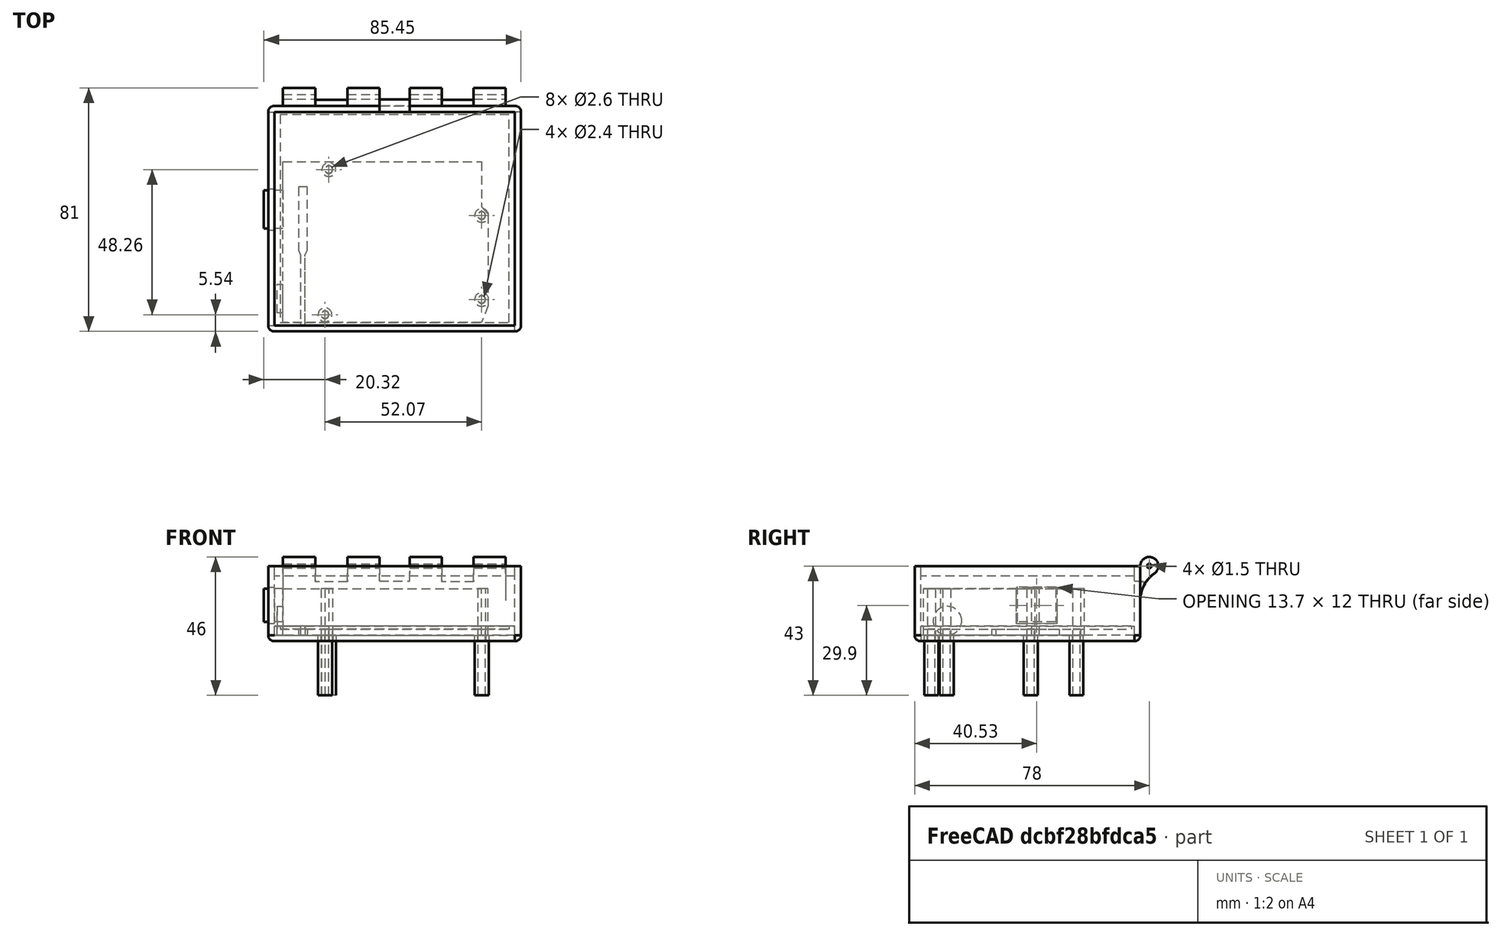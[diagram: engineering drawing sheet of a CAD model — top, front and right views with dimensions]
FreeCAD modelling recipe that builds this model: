
FCSTD DOCUMENT  (FreeCAD 1.0R39109 (Git))
Label: case_bottom_assambly
License: All rights reserved
LicenseURL: https://en.wikipedia.org/wiki/All_rights_reserved
objects: Sketcher::SketchObject×8, PartDesign::Pocket×7, App::FeaturePython×6, PartDesign::SubShapeBinder×4, PartDesign::Pad×4, PartDesign::Hole×3, Part::FeaturePython×2, PartDesign::Body×2, PartDesign::Thickness×1, Mesh::Feature×1
note: 69 computed .brp shape members not serialized (recipe doc carries the construction recipe); baked Part::Feature solids carry a one-line shape summary decoded from their .brp

FEATURE [Part::FeaturePython] b_Electronic_parts_001_  label="Electronic_parts_Eleego_001"  # a2plus imported part (geometry in sourceFile) (typed FeaturePython)
  a2p_Version = 0.4.68
  fixedPosition = true
  objectType = a2pPart
  sourceFile = ./Electronic_parts.FCStd
  sourcePart = Eleego
  subassemblyImport = false
  timeLastImport = 1.74161e+09
  updateColors = true
FEATURE [Part::FeaturePython] b_Electronic_parts_001_001  label="Electronic_parts_Keypad_001"  # a2plus imported part (geometry in sourceFile) (typed FeaturePython)
  Placement = pos=(-2.9,70,19.7) rot=(0,0,1;4.71239rad)
  a2p_Version = 0.4.68
  fixedPosition = false
  objectType = a2pPart
  sourceFile = ./Electronic_parts.FCStd
  sourcePart = Keypad
  subassemblyImport = false
  timeLastImport = 1.74161e+09
  updateColors = true
FEATURE [App::FeaturePython] axisPlaneParallel_001  label="axisPlaneParallel_001__Electronic_parts_Eleego_001"  # a2plus constraint (typed FeaturePython)
  Object1 = b_Electronic_parts_001_001
  Object2 = b_Electronic_parts_001_
  ParentTreeObject = -> b_Electronic_parts_001_001
  SubElement1 = Edge7
  SubElement2 = Face15
  Suppressed = false
  Type = axisPlaneParallel
FEATURE [App::FeaturePython] axisPlaneParallel_001_mirror  label="axisPlaneParallel_001__Electronic_parts_Keypad_001"  # a2plus constraint (typed FeaturePython)
  Object1 = b_Electronic_parts_001_001
  Object2 = b_Electronic_parts_001_
  ParentTreeObject = -> b_Electronic_parts_001_
  SubElement1 = Edge7
  SubElement2 = Face15
  Suppressed = false
  Type = axisPlaneParallel
FEATURE [App::FeaturePython] planeCoincident_001  label="planeCoincident_001__Electronic_parts_Eleego_001"  # a2plus constraint (typed FeaturePython)
  Object1 = b_Electronic_parts_001_001
  Object2 = b_Electronic_parts_001_
  ParentTreeObject = -> b_Electronic_parts_001_001
  SubElement1 = Face2
  SubElement2 = Face15
  Suppressed = false
  Type = plane
  directionConstraint = 0
  offset = 0
FEATURE [App::FeaturePython] planeCoincident_001_mirror  label="planeCoincident_001__Electronic_parts_Keypad_001"  # a2plus constraint (typed FeaturePython)
  Object1 = b_Electronic_parts_001_001
  Object2 = b_Electronic_parts_001_
  ParentTreeObject = -> b_Electronic_parts_001_
  SubElement1 = Face2
  SubElement2 = Face15
  Suppressed = false
  Type = plane
  directionConstraint = 0
  offset = 0
FEATURE [App::FeaturePython] planeCoincident_002  label="planeCoincident_002__Electronic_parts_Keypad_001"  # a2plus constraint (typed FeaturePython)
  Object1 = b_Electronic_parts_001_
  Object2 = b_Electronic_parts_001_001
  ParentTreeObject = -> b_Electronic_parts_001_
  SubElement1 = Face6
  SubElement2 = Face3
  Suppressed = false
  Type = plane
  directionConstraint = 1
  offset = 0
FEATURE [App::FeaturePython] planeCoincident_002_mirror  label="planeCoincident_002__Electronic_parts_Eleego_001"  # a2plus constraint (typed FeaturePython)
  Object1 = b_Electronic_parts_001_
  Object2 = b_Electronic_parts_001_001
  ParentTreeObject = -> b_Electronic_parts_001_001
  SubElement1 = Face6
  SubElement2 = Face3
  Suppressed = false
  Type = plane
  directionConstraint = 1
  offset = 0
FEATURE [PartDesign::SubShapeBinder] Binder
  BindCopyOnChange = 0
  BindMode = 0
  ClaimChildren = false
  Context = -> Body [Binder.]
  Fuse = false
  MakeFace = true
  OffsetFill = false
  OffsetIntersection = false
  OffsetJoinType = 0
  OffsetOpenResult = false
  PartialLoad = false
  Refine = true
  Relative = true
  Support = -> [b_Electronic_parts_001_001[Edge8,Edge5,Edge2,Edge1]]
  _Version = 2
FEATURE [Sketcher::SketchObject] Sketch
  ArcFitTolerance = 1e-06
  AttachmentSupport = -> [XY_Plane]
  ExternalGeometry = -> [Binder]
  FullyConstrained = true
  MakeInternals = false
  MapMode = 5
  sketch-geometry (4):
    g0: LineSegment StartX=-2.9 StartY=70 StartZ=0 EndX=-2.9 EndY=-1 EndZ=0
    g1: LineSegment StartX=-2.9 StartY=-1 StartZ=0 EndX=77.1 EndY=-1 EndZ=0
    g2: LineSegment StartX=77.1 StartY=-1 StartZ=0 EndX=77.1 EndY=70 EndZ=0
    g3: LineSegment StartX=77.1 StartY=70 StartZ=0 EndX=-2.9 EndY=70 EndZ=0
  constraints (10):
    c: Coincident(g0,g1)
    c: Coincident(g1,g2)
    c: Coincident(g2,g3)
    c: Coincident(g3,g0)
    c: Vertical(g0)
    c: Vertical(g2)
    c: Horizontal(g1)
    c: Horizontal(g3)
    c: Coincident(g0,g-4)
    c: Coincident(g1,g-5)
FEATURE [PartDesign::Pad] Pad
  Direction = (0,0,1)
  Length = 23
  Length2 = 10
  Profile = -> Sketch
  ReferenceAxis = -> Sketch [N_Axis]
  Refine = true
  Suppressed = false
  Type = 0
FEATURE [PartDesign::Thickness] Thickness
  Base = -> Pad [Face6]
  BaseFeature = -> Pad
  Intersection = false
  Join = 0
  Mode = 0
  Refine = true
  SupportTransform = false
  Suppressed = false
  Value = 2
FEATURE [PartDesign::SubShapeBinder] Binder001
  BindCopyOnChange = 0
  BindMode = 0
  ClaimChildren = false
  Context = -> Body [Binder001.]
  Fuse = false
  MakeFace = true
  Offset = 0.5
  OffsetFill = false
  OffsetIntersection = false
  OffsetJoinType = 0
  OffsetOpenResult = false
  PartialLoad = false
  Refine = true
  Relative = true
  Support = -> [b_Electronic_parts_001_[Face18]]
  _Version = 2
FEATURE [PartDesign::Pocket] Pocket
  BaseFeature = -> Thickness
  Direction = (1,0,0)
  Length = 5
  Length2 = 5
  Profile = -> Binder001
  Refine = true
  Suppressed = false
  Type = 0
FEATURE [PartDesign::SubShapeBinder] Binder002
  BindCopyOnChange = 0
  BindMode = 0
  ClaimChildren = false
  Context = -> Body [Binder002.]
  Fuse = false
  MakeFace = true
  OffsetFill = false
  OffsetIntersection = false
  OffsetJoinType = 0
  OffsetOpenResult = false
  PartialLoad = false
  Refine = true
  Relative = true
  Support = -> [b_Electronic_parts_001_[Edge34,Edge33,Edge32,Edge31]]
  _Version = 2
FEATURE [PartDesign::Pocket] Pocket001
  BaseFeature = -> Pocket
  Direction = (0,0,-1)
  Length = 0
  Length2 = 5
  Profile = -> Binder002
  Refine = true
  Suppressed = false
  Type = 3
  UpToFace = -> Pocket [Face31]
FEATURE [Sketcher::SketchObject] Sketch001
  ArcFitTolerance = 1e-06
  AttachmentSupport = -> [Pocket001]
  ExternalGeometry = -> [Pocket001]
  FullyConstrained = true
  MakeInternals = false
  MapMode = 5
  Placement = pos=(0,70,0) rot=(1,0,0;1.5708rad)
  sketch-geometry (6):
    g0: LineSegment StartX=32.1 StartY=23 StartZ=0 EndX=32.1 EndY=18 EndZ=0
    g1: LineSegment StartX=32.1 StartY=18 StartZ=0 EndX=42.1 EndY=18 EndZ=0
    g2: LineSegment StartX=42.1 StartY=18 StartZ=0 EndX=42.1 EndY=23 EndZ=0
    g3: LineSegment StartX=42.1 StartY=23 StartZ=0 EndX=32.1 EndY=23 EndZ=0
    g4: LineSegment [constr] StartX=-2.9 StartY=23 StartZ=0 EndX=32.1 EndY=23 EndZ=0
    g5: LineSegment [constr] StartX=42.1 StartY=23 StartZ=0 EndX=77.1 EndY=23 EndZ=0
  constraints (16):
    c: Coincident(g0,g1)
    c: Coincident(g1,g2)
    c: Coincident(g2,g3)
    c: Coincident(g3,g0)
    c: Vertical(g0)
    c: Vertical(g2)
    c: Horizontal(g1)
    c: Horizontal(g3)
    c: PointOnObject(g0,g-3)
    c: Coincident(g4,g-3)
    c: Coincident(g4,g0)
    c: Coincident(g5,g2)
    c: Coincident(g5,g-3)
    c: Equal(g5,g4)
    c: DistanceX(g1,g1) = 10
    c: DistanceY(g2,g2) = 5
FEATURE [PartDesign::Pocket] Pocket002
  BaseFeature = -> Pocket001
  Direction = (0,1,-2e-16)
  Length = 0
  Length2 = 5
  Profile = -> Sketch001
  ReferenceAxis = -> Sketch001 [N_Axis]
  Refine = true
  Suppressed = false
  Type = 3
  UpToFace = -> Pocket001 [Face20]
FEATURE [PartDesign::SubShapeBinder] Binder004
  BindCopyOnChange = 0
  BindMode = 0
  ClaimChildren = false
  Context = -> Body001 [Binder004.]
  Fuse = false
  MakeFace = true
  OffsetFill = false
  OffsetIntersection = false
  OffsetJoinType = 0
  OffsetOpenResult = false
  PartialLoad = false
  Refine = true
  Relative = true
  Support = -> [Body[Pocket002.Edge24,Pocket002.Edge25,Pocket002.Edge23,Pocket002.Vertex20,Pocket002.Edge22]]
  _Version = 2
FEATURE [Sketcher::SketchObject] Sketch002
  ArcFitTolerance = 1e-06
  AttachmentSupport = -> [XY_Plane001]
  ExternalGeometry = -> [Binder004]
  FullyConstrained = true
  MakeInternals = false
  MapMode = 5
  sketch-geometry (8):
    g0: LineSegment StartX=-2.9 StartY=70 StartZ=0 EndX=-2.9 EndY=-1 EndZ=0
    g1: LineSegment StartX=-2.9 StartY=-1 StartZ=0 EndX=77.1 EndY=-1 EndZ=0
    g2: LineSegment StartX=77.1 StartY=-1 StartZ=0 EndX=77.1 EndY=70 EndZ=0
    g3: LineSegment StartX=77.1 StartY=70 StartZ=0 EndX=-2.9 EndY=70 EndZ=0
    g4: Circle CenterX=15.24 CenterY=50.8 CenterZ=0 NormalX=0 NormalY=0 NormalZ=1 AngleXU=0 Radius=2.3
    g5: Circle CenterX=66.04 CenterY=35.56 CenterZ=0 NormalX=0 NormalY=0 NormalZ=1 AngleXU=0 Radius=2.3
    g6: Circle CenterX=66.04 CenterY=7.62 CenterZ=0 NormalX=0 NormalY=0 NormalZ=1 AngleXU=0 Radius=2.3
    g7: Circle CenterX=13.97 CenterY=2.54 CenterZ=0 NormalX=0 NormalY=0 NormalZ=1 AngleXU=0 Radius=2.3
  constraints (18):
    c: Coincident(g0,g1)
    c: Coincident(g1,g2)
    c: Coincident(g2,g3)
    c: Coincident(g3,g0)
    c: Vertical(g0)
    c: Vertical(g2)
    c: Horizontal(g1)
    c: Horizontal(g3)
    c: Coincident(g0,g-7)
    c: Coincident(g1,g-5)
    c: Coincident(g4,g-8)
    c: Radius(g4) = 2.3
    c: Coincident(g5,g-9)
    c: Coincident(g6,g-10)
    c: Coincident(g7,g-11)
    c: Equal(g4,g5)
    c: Equal(g5,g6)
    c: Equal(g6,g7)
FEATURE [PartDesign::Pad] Pad001
  Direction = (0,0,1)
  Length = 3
  Length2 = 10
  Profile = -> Sketch002 [Edge4,Edge3,Edge2,Edge1]
  ReferenceAxis = -> Sketch002 [N_Axis]
  Refine = true
  Suppressed = false
  Type = 0
FEATURE [PartDesign::Pad] Pad002
  BaseFeature = -> Pad001
  Direction = (0,0,1)
  Length = 20
  Length2 = 10
  Profile = -> Sketch002 [Edge8,Edge5,Edge6,Edge7]
  ReferenceAxis = -> Sketch002 [N_Axis]
  Refine = true
  Reversed = true
  Suppressed = false
  Type = 0
FEATURE [PartDesign::Hole] Hole
  BaseFeature = -> Pad002
  CustomThreadClearance = 0
  Depth = 25
  DepthType = 0
  Diameter = 2.4
  DrillForDepth = false
  DrillPoint = 1
  DrillPointAngle = 118
  HoleCutCountersinkAngle = 90
  HoleCutCustomValues = false
  HoleCutDepth = 0
  HoleCutDiameter = 6.1
  HoleCutType = 0
  ModelThread = false
  Profile = -> Pad002 [Face13]
  Refine = true
  Suppressed = false
  Tapered = false
  TaperedAngle = 90
  ThreadClass = 0
  ThreadDepth = 25
  ThreadDepthType = 0
  ThreadDirection = 0
  ThreadFit = 0
  ThreadSize = 0
  ThreadType = 0
  Threaded = false
  UseCustomThreadClearance = false
FEATURE [PartDesign::Hole] Hole001
  BaseFeature = -> Hole
  CustomThreadClearance = 0
  Depth = 25
  DepthType = 0
  Diameter = 2.4
  DrillForDepth = false
  DrillPoint = 1
  DrillPointAngle = 118
  HoleCutCountersinkAngle = 90
  HoleCutCustomValues = false
  HoleCutDepth = 0
  HoleCutDiameter = 6.1
  HoleCutType = 0
  ModelThread = false
  Profile = -> Hole [Face12,Face15,Face13]
  Refine = true
  Suppressed = false
  Tapered = false
  TaperedAngle = 90
  ThreadClass = 0
  ThreadDepth = 25
  ThreadDepthType = 0
  ThreadDirection = 0
  ThreadFit = 0
  ThreadSize = 0
  ThreadType = 0
  Threaded = false
  UseCustomThreadClearance = false
FEATURE [Sketcher::SketchObject] Sketch003
  ArcFitTolerance = 1e-06
  AttachmentSupport = -> [Hole001]
  ExternalGeometry = -> [Hole001]
  FullyConstrained = true
  MakeInternals = false
  MapMode = 5
  Placement = pos=(0,0,3) rot=(0,0,1;0rad)
  sketch-geometry (8):
    g0: LineSegment StartX=-0.9 StartY=69 StartZ=0 EndX=-0.9 EndY=-2.15318e-07 EndZ=0
    g1: LineSegment StartX=-0.9 StartY=-2.15318e-07 StartZ=0 EndX=75.1 EndY=-2.15318e-07 EndZ=0
    g2: LineSegment StartX=75.1 StartY=-2.15318e-07 StartZ=0 EndX=75.1 EndY=69 EndZ=0
    g3: LineSegment StartX=75.1 StartY=69 StartZ=0 EndX=-0.9 EndY=69 EndZ=0
    g4: LineSegment [constr] StartX=-0.9 StartY=69 StartZ=0 EndX=-2.9 EndY=69 EndZ=0
    g5: LineSegment [constr] StartX=75.1 StartY=69 StartZ=0 EndX=77.1 EndY=69 EndZ=0
    g6: LineSegment [constr] StartX=-0.9 StartY=69 StartZ=0 EndX=-0.9 EndY=70 EndZ=0
    g7: LineSegment [constr] StartX=75.1 StartY=-2.15318e-07 StartZ=0 EndX=75.1 EndY=-1 EndZ=0
  constraints (24):
    c: Coincident(g0,g1)
    c: Coincident(g1,g2)
    c: Coincident(g2,g3)
    c: Coincident(g3,g0)
    c: Vertical(g0)
    c: Vertical(g2)
    c: Horizontal(g1)
    c: Horizontal(g3)
    c: Coincident(g4,g0)
    c: PointOnObject(g4,g-5)
    c: Horizontal(g4)
    c: Coincident(g5,g2)
    c: Parallel(g5,g3)
    c: Vertical(g5,g-4)
    c: Coincident(g6,g0)
    c: Coincident(g7,g1)
    c: Parallel(g7,g2)
    c: Parallel(g0,g6)
    c: Horizontal(g7,g-6)
    c: Horizontal(g6,g-5)
    c: Equal(g7,g6)
    c: Equal(g4,g5)
    c: DistanceX(g3,g3) = 76
    c: DistanceY(g2,g2) = 69
FEATURE [PartDesign::Pocket] Pocket003
  BaseFeature = -> Hole001
  Direction = (0,0,-1)
  Length = 1
  Length2 = 5
  Profile = -> Sketch003
  ReferenceAxis = -> Sketch003 [N_Axis]
  Refine = true
  Suppressed = false
  Type = 0
FEATURE [Sketcher::SketchObject] Sketch004
  ArcFitTolerance = 1e-06
  AttachmentSupport = -> [Pocket003]
  ExternalGeometry = -> [Pocket003]
  FullyConstrained = true
  MakeInternals = false
  MapMode = 5
  Placement = pos=(0,0,2) rot=(0,0,1;0rad)
  sketch-geometry (12):
    g0: LineSegment [constr] StartX=5.1 StartY=45 StartZ=0 EndX=5.1 EndY=69 EndZ=0
    g1: LineSegment StartX=5.1 StartY=45 StartZ=0 EndX=5.1 EndY=24 EndZ=0
    g2: LineSegment StartX=8.1 StartY=24 StartZ=0 EndX=8.1 EndY=45 EndZ=0
    g3: LineSegment StartX=8.1 StartY=45 StartZ=0 EndX=5.1 EndY=45 EndZ=0
    g4: LineSegment StartX=5.1 StartY=24 StartZ=0 EndX=5.85 EndY=22.5 EndZ=0
    g5: LineSegment StartX=5.85 StartY=22.5 StartZ=0 EndX=5.85 EndY=-1 EndZ=0
    g6: LineSegment StartX=5.85 StartY=-1 StartZ=0 EndX=7.35 EndY=-1 EndZ=0
    g7: LineSegment StartX=7.35 StartY=-1 StartZ=0 EndX=7.35 EndY=22.5 EndZ=0
    g8: LineSegment StartX=7.35 StartY=22.5 StartZ=0 EndX=8.1 EndY=24 EndZ=0
    g9: LineSegment [constr] StartX=7.35 StartY=22.5 StartZ=0 EndX=8.1 EndY=22.5 EndZ=0
    g10: LineSegment [constr] StartX=8.1 StartY=24 StartZ=0 EndX=8.1 EndY=22.5 EndZ=0
    g11: LineSegment [constr] StartX=5.85 StartY=22.5 StartZ=0 EndX=5.1 EndY=22.5 EndZ=0
  constraints (35):
    c: Vertical(g0)
    c: Horizontal(g0,g-3)
    c: DistanceY(g0,g0) = 24
    c: Coincident(g2,g3)
    c: Coincident(g3,g1)
    c: Vertical(g1)
    c: Vertical(g2)
    c: Horizontal(g3)
    c: Coincident(g1,g0)
    c: DistanceY(g2,g2) = 21
    c: Distance(g1,g2) = 3
    c: Coincident(g1,g4)
    c: Coincident(g4,g5)
    c: Vertical(g5)
    c: Coincident(g5,g6)
    c: Horizontal(g6)
    c: Coincident(g6,g7)
    c: Vertical(g7)
    c: Coincident(g7,g8)
    c: Coincident(g8,g2)
    c: Distance(g6,g6) = 1.5
    c: Horizontal(g4,g7)
    c: Horizontal(g1,g2)
    c: Coincident(g9,g7)
    c: Horizontal(g9)
    c: Vertical(g2,g9)
    c: Coincident(g10,g2)
    c: Coincident(g10,g9)
    c: DistanceY(g10,g10) = 1.5
    c: Coincident(g11,g4)
    c: Horizontal(g11)
    c: Vertical(g11,g1)
    c: Equal(g11,g9)
    c: Horizontal(g5,g-5)
    c: Distance(g0,g-3) = 6
FEATURE [PartDesign::Pocket] Pocket004
  BaseFeature = -> Pocket003
  Direction = (0,0,-1)
  Length = 5
  Length2 = 5
  Midplane = true
  Profile = -> Sketch004
  ReferenceAxis = -> Sketch004 [N_Axis]
  Refine = true
  Suppressed = false
  Type = 0
FEATURE [PartDesign::Body] Body001  label="keypad_holder"
  AllowCompound = false
  Group = -> [Sketch002,Pad001,Binder004,Pad002,Hole,Hole001,Sketch003,Pocket003,Sketch004,Pocket004]
  Origin = -> Origin001
  Tip = -> Pocket004
FEATURE [Mesh::Feature] Mesh001  label="Pocket004 (Meshed)"
FEATURE [Sketcher::SketchObject] Sketch005
  ArcFitTolerance = 1e-06
  AttachmentSupport = -> [Pocket002]
  ExternalGeometry = -> [Pocket002]
  FullyConstrained = true
  MakeInternals = false
  MapMode = 4
  Placement = pos=(0,0,0) rot=(0.57735,0.57735,0.57735;2.0944rad)
  sketch-geometry (4):
    g0: ArcOfCircle CenterX=75 CenterY=23 CenterZ=0 NormalX=0 NormalY=0 NormalZ=1 AngleXU=0 Radius=3 StartAngle=5.32182 EndAngle=9.42478
    g1: ArcOfCircle CenterX=83.0318 CenterY=11.4943 CenterZ=0 NormalX=0 NormalY=0 NormalZ=1 AngleXU=0 Radius=11.0318 StartAngle=2.18023 EndAngle=3.14159
    g2: LineSegment StartX=72 StartY=23 StartZ=0 EndX=72 EndY=11.4943 EndZ=0
    g3: LineSegment [constr] StartX=72 StartY=11.4943 StartZ=0 EndX=72 EndY=0 EndZ=0
  constraints (8):
    c: Tangent(g-3,g0) = 1.5708
    c: Tangent(g0,g1) = 1.5708
    c: Coincident(g2,g0)
    c: Tangent(g2,g1) = -1.5708
    c: Vertical(g2)
    c: Radius(g0) = 3
    c: Tangent(g3,g1) = -1.5708
    c: Coincident(g3,g-3)
FEATURE [PartDesign::Pad] Pad003
  BaseFeature = -> Pocket002
  Direction = (1,0,0)
  Length = 74
  Length2 = 10
  Profile = -> Sketch005 [Edge1,Edge2,Edge3]
  ReferenceAxis = -> Sketch005 [N_Axis]
  Refine = true
  Suppressed = false
  Type = 0
FEATURE [PartDesign::Hole] Hole002
  BaseFeature = -> Pad003
  CustomThreadClearance = 0
  Depth = 242.398
  DepthType = 1
  Diameter = 1.5
  DrillForDepth = false
  DrillPoint = 1
  DrillPointAngle = 118
  HoleCutCountersinkAngle = 90
  HoleCutCustomValues = false
  HoleCutDepth = 0
  HoleCutDiameter = 6.1
  HoleCutType = 0
  ModelThread = false
  Profile = -> Pad003 [Face34]
  Refine = true
  Suppressed = false
  Tapered = false
  TaperedAngle = 90
  ThreadClass = 0
  ThreadDepth = 242.398
  ThreadDepthType = 0
  ThreadDirection = 0
  ThreadFit = 0
  ThreadSize = 0
  ThreadType = 0
  Threaded = false
  UseCustomThreadClearance = false
FEATURE [Sketcher::SketchObject] Sketch006
  ArcFitTolerance = 1e-06
  AttachmentSupport = -> [Hole002]
  ExternalGeometry = -> [Hole002]
  FullyConstrained = true
  MakeInternals = false
  MapMode = 5
  Placement = pos=(0,70,0) rot=(1,0,0;1.5708rad)
  sketch-geometry (4):
    g0: LineSegment StartX=32.1 StartY=18 StartZ=0 EndX=42.1 EndY=18 EndZ=0
    g1: LineSegment StartX=42.1 StartY=18 StartZ=0 EndX=42.1 EndY=33 EndZ=0
    g2: LineSegment StartX=42.1 StartY=33 StartZ=0 EndX=32.1 EndY=33 EndZ=0
    g3: LineSegment StartX=32.1 StartY=33 StartZ=0 EndX=32.1 EndY=18 EndZ=0
  constraints (11):
    c: Coincident(g0,g1)
    c: Coincident(g1,g2)
    c: Coincident(g2,g3)
    c: Coincident(g3,g0)
    c: Horizontal(g0)
    c: Horizontal(g2)
    c: Vertical(g1)
    c: Vertical(g3)
    c: Coincident(g0,g-3)
    c: Vertical(g0,g-4)
    c: DistanceY(g1,g1) = 15
FEATURE [PartDesign::Pocket] Pocket005
  BaseFeature = -> Hole002
  Direction = (0,1,-2e-16)
  Length = 9
  Length2 = 5
  Profile = -> Sketch006
  ReferenceAxis = -> Sketch006 [N_Axis]
  Refine = true
  Suppressed = false
  Type = 0
FEATURE [Sketcher::SketchObject] Sketch007
  ArcFitTolerance = 1e-06
  AttachmentSupport = -> [Pocket005]
  ExternalGeometry = -> [Pocket005]
  FullyConstrained = true
  MakeInternals = false
  MapMode = 5
  Placement = pos=(0,72,0) rot=(0,0.707107,0.707107;3.14159rad)
  sketch-geometry (12):
    g0: LineSegment StartX=-63.35 StartY=26 StartZ=0 EndX=-52.75 EndY=26 EndZ=0
    g1: LineSegment StartX=-21.35 StartY=26 StartZ=0 EndX=-10.75 EndY=26 EndZ=0
    g2: LineSegment StartX=-63.35 StartY=26 StartZ=0 EndX=-63.35 EndY=17.8 EndZ=0
    g3: LineSegment StartX=-52.75 StartY=26 StartZ=0 EndX=-52.75 EndY=17.8 EndZ=0
    g4: LineSegment StartX=-63.35 StartY=17.8 StartZ=0 EndX=-52.75 EndY=17.8 EndZ=0
    g5: LineSegment [constr] StartX=-74 StartY=26 StartZ=0 EndX=-63.35 EndY=26 EndZ=0
    g6: LineSegment [constr] StartX=-52.75 StartY=26 StartZ=0 EndX=-42.1 EndY=26 EndZ=0
    g7: LineSegment StartX=-21.35 StartY=26 StartZ=0 EndX=-21.35 EndY=17.8 EndZ=0
    g8: LineSegment StartX=-10.75 StartY=26 StartZ=0 EndX=-10.75 EndY=17.8 EndZ=0
    g9: LineSegment StartX=-21.35 StartY=17.8 StartZ=0 EndX=-10.75 EndY=17.8 EndZ=0
    g10: LineSegment [constr] StartX=-32.1 StartY=26 StartZ=0 EndX=-21.35 EndY=26 EndZ=0
    g11: LineSegment [constr] StartX=-10.75 StartY=26 StartZ=0 EndX=0 EndY=26 EndZ=0
  constraints (34):
    c: Horizontal(g0)
    c: Horizontal(g1)
    c: Horizontal(g-6,g0)
    c: Horizontal(g-3,g1)
    c: Distance(g-6,g-4) = 31.9
    c: Coincident(g2,g0)
    c: Vertical(g2)
    c: Coincident(g3,g0)
    c: Vertical(g3)
    c: Coincident(g4,g2)
    c: Coincident(g4,g3)
    c: Parallel(g4,g0)
    c: Coincident(g5,g-6)
    c: Coincident(g5,g0)
    c: Coincident(g6,g0)
    c: Coincident(g6,g-4)
    c: Equal(g5,g6)
    c: DistanceX(g4,g4) = 10.6
    c: Distance(g-6,g-6) = 5.45992
    c: Coincident(g7,g1)
    c: Vertical(g7)
    c: Coincident(g8,g1)
    c: Vertical(g8)
    c: Coincident(g9,g7)
    c: Coincident(g9,g8)
    c: Horizontal(g9)
    c: Coincident(g10,g-3)
    c: Coincident(g10,g1)
    c: Coincident(g11,g1)
    c: Coincident(g11,g-5)
    c: Equal(g11,g10)
    c: Equal(g3,g7)
    c: Equal(g1,g0)
    c: DistanceY(g7,g7) = 8.2
FEATURE [PartDesign::Pocket] Pocket006
  BaseFeature = -> Pocket005
  Direction = (0,-1,2e-16)
  Length = 9
  Length2 = 5
  Profile = -> Sketch007
  ReferenceAxis = -> Sketch007 [N_Axis]
  Refine = true
  Reversed = true
  Suppressed = false
  Type = 0
FEATURE [PartDesign::Body] Body  label="case"
  AllowCompound = false
  Group = -> [Sketch,Binder,Pad,Thickness,Binder001,Pocket,Binder002,Pocket001,Sketch001,Pocket002,Sketch005,Pad003,Hole002,Sketch006,Pocket005,Sketch007,Pocket006]
  Origin = -> Origin
  Tip = -> Pocket006
